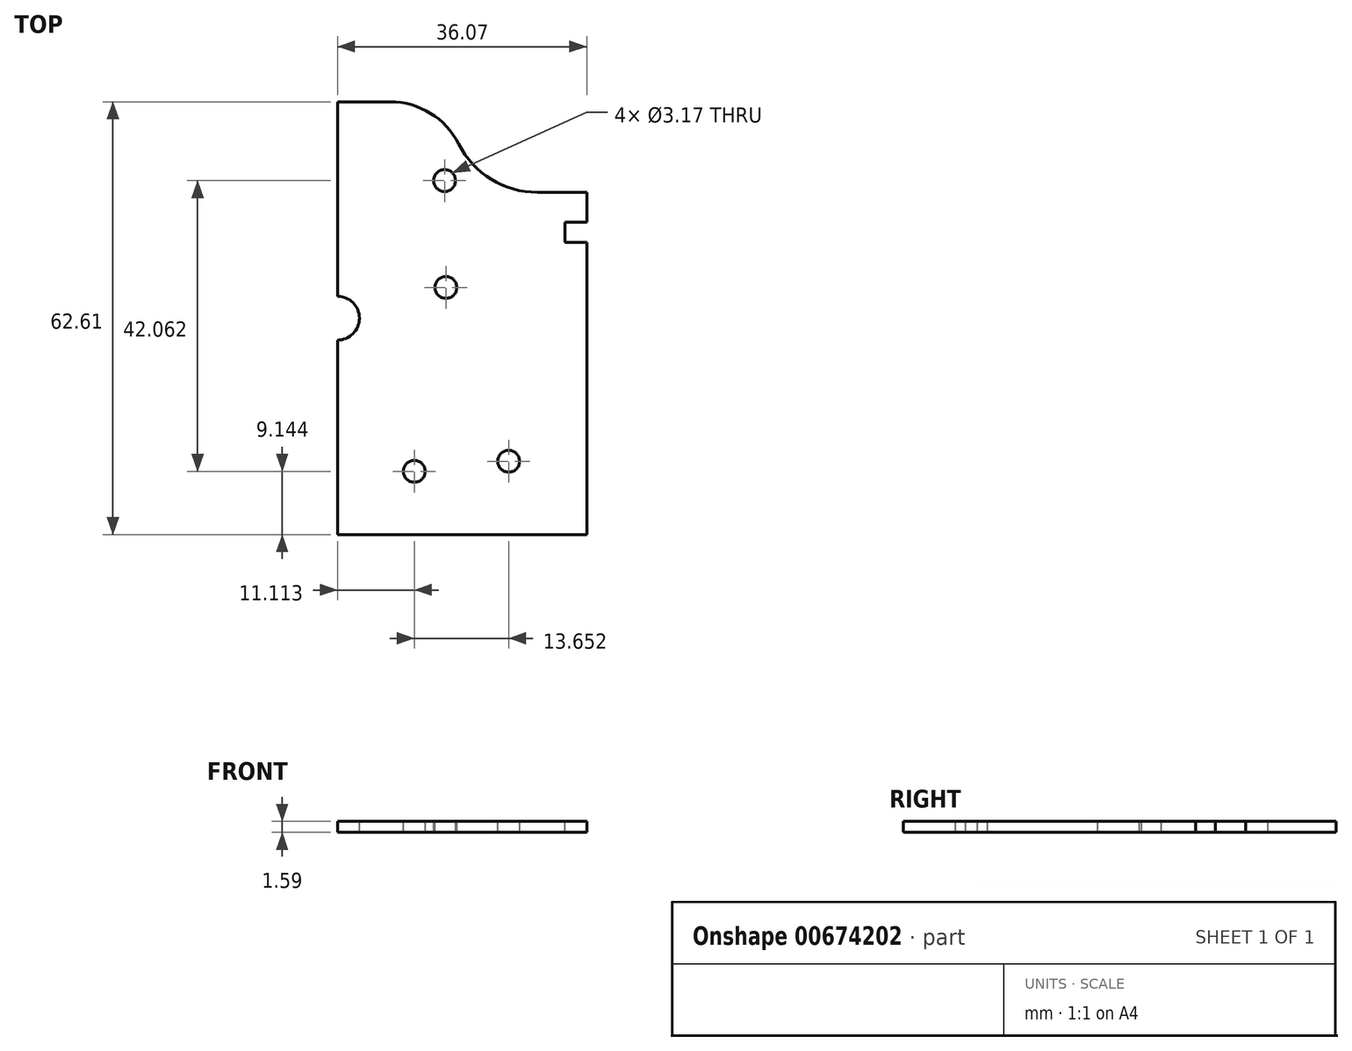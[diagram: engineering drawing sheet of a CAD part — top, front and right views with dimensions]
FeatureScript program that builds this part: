
annotation { "Feature Type Name" : "Feature", "Feature Type Description" : "" }
export const myFeature = defineFeature(function(context is Context, id is Id, definition is map)
    precondition{}
    {
        {
            var Q0;
            Q0=qCreatedBy(makeId("Top.planeOp"),FACE);
            var sketch = newSketch(context, id + "F0", { "sketchPlane" : qUnion([Q0])});
            skLineSegment(sketch, "E0", {"start": v(0, 0) * mm, "end": v(0, 62.61) * mm});
            skLineSegment(sketch, "E1", {"start": v(0, 62.61) * mm, "end": v(7.62, 62.61) * mm});
            skLineSegment(sketch, "E2", {"start": v(28.93, 49.5) * mm, "end": v(36.07, 49.53) * mm});
            skLineSegment(sketch, "E3", {"start": v(36.07, 49.53) * mm, "end": v(36.07, 0) * mm});
            skLineSegment(sketch, "E4", {"start": v(36.07, 0) * mm, "end": v(0, 0) * mm});
            skArc(sketch, "E5.filletArc", {"start": v(17.55, 56.5) * mm, "mid": v(13.45, 60.96) * mm, "end": v(7.62, 62.61) * mm});
            skArc(sketch, "E6.filletArc", {"start": v(17.55, 56.5) * mm, "mid": v(22.24, 51.38) * mm, "end": v(28.93, 49.5) * mm});
            skPoint(sketch, "E7", {"position": v(24.77, 10.6) * mm});
            skPoint(sketch, "E8", {"position": v(15.68, 35.75) * mm});
            skPoint(sketch, "E9", {"position": v(15.5, 51.2) * mm});
            skLineSegment(sketch, "E10.bottom", {"start": v(36.07, 42.3) * mm, "end": v(32.9, 42.3) * mm});
            skLineSegment(sketch, "E10.top", {"start": v(36.07, 45.16) * mm, "end": v(32.9, 45.16) * mm});
            skLineSegment(sketch, "E10.left", {"start": v(36.07, 42.3) * mm, "end": v(36.07, 45.16) * mm});
            skLineSegment(sketch, "E10.right", {"start": v(32.9, 42.3) * mm, "end": v(32.9, 45.16) * mm});
            skCircle(sketch, "E11", {"center": v(0, 31.3) * mm, "radius": 3.18 * mm});
            skPoint(sketch, "E12", {"position": v(11.11, 9.14) * mm});
            skSolve(sketch);
        }
        {
            var Q0;
            {var subQ9=sQuery(id+"F0.wireOp",EDGE,"E1");Q0=makeQuery(id+"F0.imprint","IMPRINT",FACE,{"disambiguationData":[TD([[makeQuery(id+"F0.imprint","IMPRINT",EDGE,{"derivedFrom":subQ9}),-1.0]])]});}
            extrude(context, id + "F1", {"entities" : qUnion([Q0]), "oppositeDirection" : true, "depth" : 1.59 * mm, "offsetDistance" : 25.4 * mm});
        }
        {
            var Q0;
            Q0=sQuery(id+"F0.wireOp",VERTEX,"E9");
            var Q1;
            Q1=sQuery(id+"F0.wireOp",VERTEX,"E8");
            var Q2;
            Q2=sQuery(id+"F0.wireOp",VERTEX,"E12");
            var Q3;
            Q3=sQuery(id+"F0.wireOp",VERTEX,"E7");
            var Q4;
            Q4=makeQuery(id+"F1.opExtrude","SWEPT_BODY",BODY,{"disambiguationData":[OSD([sQuery(id+"F0.wireOp",EDGE,"E0"),sQuery(id+"F0.wireOp",EDGE,"E1"),sQuery(id+"F0.wireOp",EDGE,"E2"),sQuery(id+"F0.wireOp",EDGE,"E3"),sQuery(id+"F0.wireOp",EDGE,"E4"),sQuery(id+"F0.wireOp",EDGE,"E5.filletArc"),sQuery(id+"F0.wireOp",EDGE,"E6.filletArc"),sQuery(id+"F0.wireOp",EDGE,"E10.bottom"),sQuery(id+"F0.wireOp",EDGE,"E10.top"),sQuery(id+"F0.wireOp",EDGE,"E10.right"),sQuery(id+"F0.wireOp",EDGE,"E11")])]});
            hole(context, id + "F2", {"style" : HoleStyle.SIMPLE, "endStyle" : HoleEndStyle.THROUGH, "holeDiameter" : 3.17 * mm, "majorDiameter" : 6.35 * mm, "tappedDepth" : 12.7 * mm, "tapClearance" : 3, "locations" : qUnion([Q0, Q1, Q2, Q3]), "scope" : qUnion([Q4])});
        }
    });
